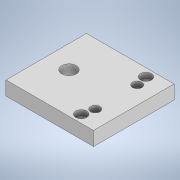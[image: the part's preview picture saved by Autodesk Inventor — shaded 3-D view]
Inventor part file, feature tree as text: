
AUTODESK INVENTOR PART (.ipt)
format: ipt  version: 2022 (Build 260153000, 153)  size: 150,016 bytes
history: native  units: mm
features: extrude x4, sketch x4, projected_geometry x1
ambient origin geometry x8: Origin, YZ Plane, XZ Plane, XY Plane, X Axis, Y Axis, Z Axis, Center Point
bodies: Solid1 (feature_tree)
feature tree (9):
  extrude  "Extrusion1"  Depth=50.0mm
  extrude  "Extrusion2"  Depth=13.0mm
  extrude  "Extrusion3"  Depth=11.0mm
  extrude  "Extrusion5"  Depth=1.0mm
  sketch  "Sketch1"  dims[d0=46.0mm d1=50.0mm]
  sketch  "Sketch2"  dims[d2=23.0mm d3=13.0mm]
  projected_geometry  "Projected Loop1"
  sketch  "Sketch3"  dims[d4=8.3mm d5=11.0mm]
  sketch  "Sketch5"  dims[d6=10.0mm d7=5.3mm d8=8.0mm d9=0.0mm d10=10.0mm d11=10.0mm d12=5.0mm d13=0.0mm d14=4.5mm d15=11.5mm d16=6.3mm d17=3.0mm d18=0.0mm d21=1.0mm d22=0.0mm]
